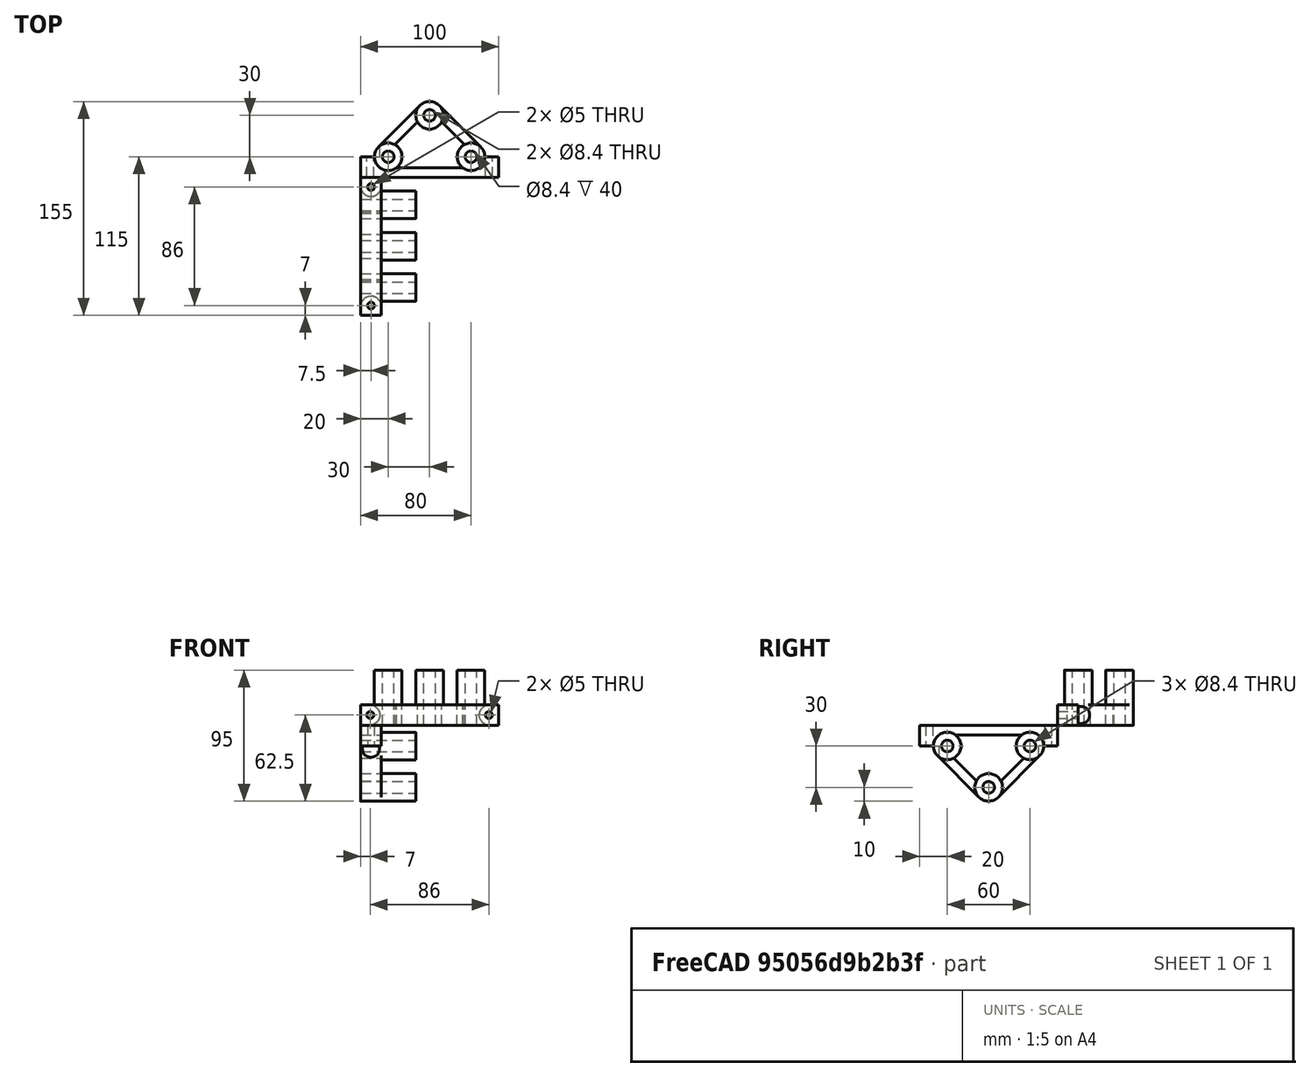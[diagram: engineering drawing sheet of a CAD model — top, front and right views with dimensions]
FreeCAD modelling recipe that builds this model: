
FCSTD DOCUMENT  (FreeCAD 0.15R4527 (Git))
Label: y_frame_outside
License: All rights reserved
LicenseURL: http://es.wikipedia.org/wiki/Todos_los_derechos_reservados
objects: Part::Cylinder×10, Part::MultiFuse×6, Part::Cut×4, Part::Box×2, Part::Feature×2, Sketcher::SketchObject×1, Part::Extrusion×1, Mesh::Feature×1
note: 26 computed .brp shape members not serialized (recipe doc carries the construction recipe); baked Part::Feature solids carry a one-line shape summary decoded from their .brp

FEATURE [Part::Box] Box  label="Cubo"
  Height = 15
  Length = 100
  Width = 15
FEATURE [Part::Cylinder] Cylinder  label="Cilindro"
  Angle = 360
  Height = 40
  Placement = pos=(20,15,0) rot=(0,0,-1;0.785398rad)
  Radius = 10
FEATURE [Part::Cylinder] Cylinder001  label="Cilindro001"
  Angle = 360
  Height = 40
  Placement = pos=(80,15,0) rot=(0,0,-1;0.785398rad)
  Radius = 10
FEATURE [Part::Cylinder] Cylinder002  label="Cilindro002"
  Angle = 360
  Height = 40
  Placement = pos=(50,45,0) rot=(0,0,-1;0.785398rad)
  Radius = 10
FEATURE [Part::MultiFuse] Fusion
  Shapes = -> [Cylinder,Cylinder001,Cylinder002]
FEATURE [Part::Box] Box001  label="Cubo001"
  Height = 15
  Length = 55
  Placement = pos=(24,7,0) rot=(0,0,1;0rad)
  Width = 8
FEATURE [Part::Cut] Cut
  Base = -> Box
  Tool = -> Box001
FEATURE [Part::MultiFuse] Fusion001
  Shapes = -> [Fusion,Cut]
FEATURE [Sketcher::SketchObject] Sketch
  ExternalGeometry = -> [Fusion001]
  Placement = pos=(0,0,0) rot=(1,0,0;3.14159rad)
  Support = -> Fusion001 [Face11]
  sketch-geometry (10):
    g0: LineSegment StartX=12.9289 StartY=-22.0711 StartZ=0 EndX=42.9289 EndY=-52.0711 EndZ=0
    g1: LineSegment StartX=24.624 StartY=-23.8667 StartZ=0 EndX=41.1333 EndY=-40.376 EndZ=0
    g2: LineSegment [constr] StartX=24.624 StartY=-23.8667 StartZ=0 EndX=19.6743 EndY=-28.8164 EndZ=0
    g3: LineSegment StartX=57.0711 StartY=-52.0711 StartZ=0 EndX=87.0711 EndY=-22.0711 EndZ=0
    g4: LineSegment StartX=58.8667 StartY=-40.376 StartZ=0 EndX=75.376 EndY=-23.8667 EndZ=0
    g5: LineSegment [constr] StartX=75.376 StartY=-23.8667 StartZ=0 EndX=80.3257 EndY=-28.8164 EndZ=0
    g6: ArcOfCircle CenterX=50 CenterY=-45 CenterZ=0 NormalX=0 NormalY=0 NormalZ=1 Radius=10 StartAngle=2.66089 EndAngle=3.92699
    g7: ArcOfCircle CenterX=20 CenterY=-15 CenterZ=0 NormalX=0 NormalY=0 NormalZ=1 Radius=10 StartAngle=3.92699 EndAngle=5.19309
    g8: ArcOfCircle CenterX=80 CenterY=-15 CenterZ=0 NormalX=0 NormalY=0 NormalZ=1 Radius=10 StartAngle=4.23168 EndAngle=5.49779
    g9: ArcOfCircle CenterX=50 CenterY=-45 CenterZ=0 NormalX=0 NormalY=0 NormalZ=1 Radius=10 StartAngle=5.49779 EndAngle=6.76389
  constraints (30):
    c: Tangent(g0,g-3) = -1.5708
    c: Tangent(g0,g-4) = -1.5708
    c: PointOnObject(g1,g-4)
    c: PointOnObject(g1,g-3)
    c: Parallel(g1,g0)
    c: Coincident(g2,g1)
    c: PointOnObject(g2,g0)
    c: Perpendicular(g0,g2)
    c: Distance(g2) = 7
    c: Tangent(g3,g-5) = -1.5708
    c: Tangent(g3,g-3) = -1.5708
    c: PointOnObject(g4,g-3)
    c: PointOnObject(g4,g-5)
    c: Parallel(g4,g3)
    c: Coincident(g5,g4)
    c: PointOnObject(g5,g3)
    c: Perpendicular(g3,g5)
    c: Equal(g5,g2)
    c: Coincident(g6,g-3)
    c: Coincident(g6,g1)
    c: Coincident(g6,g0)
    c: Coincident(g7,g-4)
    c: Coincident(g7,g0)
    c: Coincident(g7,g1)
    c: Coincident(g8,g-5)
    c: Coincident(g8,g4)
    c: Coincident(g8,g3)
    c: Coincident(g9,g6)
    c: Coincident(g9,g4)
    c: Coincident(g9,g3)
FEATURE [Part::Cylinder] Cylinder003  label="Cilindro003"
  Angle = 360
  Height = 42
  Placement = pos=(20,15,-1) rot=(0,0,1;0rad)
  Radius = 4.2
FEATURE [Part::Cylinder] Cylinder004  label="Cilindro004"
  Angle = 360
  Height = 42
  Placement = pos=(50,45,-1) rot=(0,0,1;0rad)
  Radius = 4.2
FEATURE [Part::Cylinder] Cylinder005  label="Cilindro005"
  Angle = 360
  Height = 42
  Placement = pos=(80,15,-1) rot=(0,0,1;0rad)
  Radius = 4.2
FEATURE [Part::MultiFuse] Fusion002
  Shapes = -> [Cylinder003,Cylinder005,Cylinder004]
FEATURE [Part::Extrusion] Extrude001
  Base = -> Sketch
  Dir = (0,0,15)
  Solid = true
FEATURE [Part::MultiFuse] Fusion003
  Shapes = -> [Fusion001,Extrude001]
FEATURE [Part::Cut] Cut001
  Base = -> Fusion003
  Tool = -> Fusion002
FEATURE [Part::Cylinder] Cylinder006  label="Cilindro006"
  Angle = 360
  Height = 17
  Placement = pos=(7,-1,7.5) rot=(-1,0,0;1.5708rad)
  Radius = 2.5
FEATURE [Part::Cylinder] Cylinder007  label="Cilindro007"
  Angle = 360
  Height = 17
  Placement = pos=(93,-1,7.5) rot=(-1,0,0;1.5708rad)
  Radius = 2.5
FEATURE [Part::MultiFuse] Fusion004
  Shapes = -> [Cylinder006,Cylinder007]
FEATURE [Part::Cut] Cut002
  Base = -> Cut001
  Tool = -> Fusion004
FEATURE [Part::Cylinder] Cylinder008  label="Cilindro008"
  Angle = 360
  Height = 17
  Placement = pos=(7,15,7.5) rot=(-1,0,0;1.5708rad)
  Radius = 7
FEATURE [Part::Cylinder] Cylinder009  label="Cilindro009"
  Angle = 360
  Height = 17
  Placement = pos=(93,15,7.5) rot=(-1,0,0;1.5708rad)
  Radius = 7
FEATURE [Part::MultiFuse] Fusion005
  Shapes = -> [Cylinder008,Cylinder009]
FEATURE [Part::Cut] Cut003  label="y_frame_outside"
  Base = -> Cut002
  Tool = -> Fusion005
FEATURE [Mesh::Feature] frameoutside
FEATURE [Part::Feature] frameoutside002
  shape: bbox 100 x 55 x 40 mm, 2146 faces, 0 solids (baked)
FEATURE [Part::Feature] Cut004  label="y_frame_outside001"
  Placement = pos=(0,0,0) rot=(-0.57735,0.57735,-0.57735;2.0944rad)
  shape: bbox 40 x 100 x 55 mm, 29 faces (baked)
